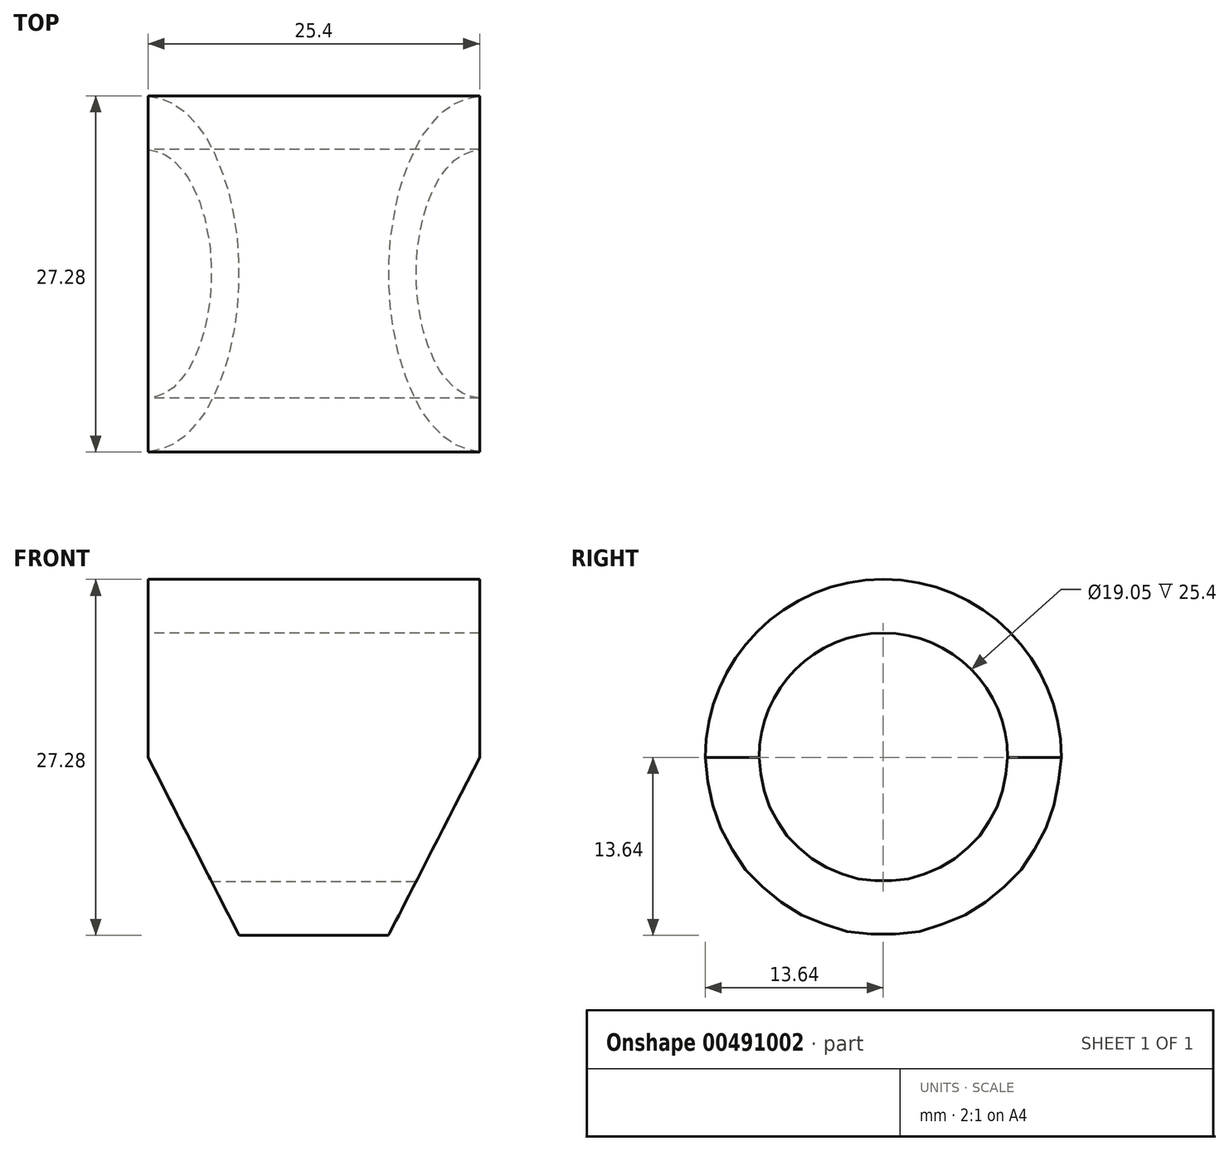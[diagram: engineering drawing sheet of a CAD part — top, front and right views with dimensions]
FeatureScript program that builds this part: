
annotation { "Feature Type Name" : "Feature", "Feature Type Description" : "" }
export const myFeature = defineFeature(function(context is Context, id is Id, definition is map)
    precondition{}
    {
        {
            var Q0;
            Q0=qCreatedBy(makeId("Right.planeOp"),FACE);
            var sketch = newSketch(context, id + "F0", { "sketchPlane" : qUnion([Q0])});
            skCircle(sketch, "E0", {"center": v(0, 0) * mm, "radius": 13.64 * mm});
            skCircle(sketch, "E1", {"center": v(0, 0) * mm, "radius": 9.53 * mm});
            skSolve(sketch);
        }
        {
            var Q0;
            Q0=makeQuery(id+"F0.imprint","IMPRINT",FACE,{"disambiguationData":[TD([[makeQuery(id+"F0.imprint","IMPRINT",EDGE,{"derivedFrom":sQuery(id+"F0.wireOp",EDGE,"E0")}),1.0]])]});
            extrude(context, id + "F1", {"entities" : qUnion([Q0]), "endBound" : BoundingType.SYMMETRIC, "depth" : 25.4 * mm});
        }
        {
            var Q0;
            Q0=qCreatedBy(makeId("Front.planeOp"),FACE);
            var sketch = newSketch(context, id + "F2", { "sketchPlane" : qUnion([Q0])});
            skLineSegment(sketch, "E2", {"start": v(-12.7, 0) * mm, "end": v(0, -24.8) * mm});
            skLineSegment(sketch, "E3", {"start": v(0, -24.8) * mm, "end": v(12.7, 0) * mm});
            skLineSegment(sketch, "E4", {"start": v(12.7, 0) * mm, "end": v(38.1, -37.9) * mm});
            skLineSegment(sketch, "E5", {"start": v(38.23, -37.66) * mm, "end": v(-20.1, -37.9) * mm});
            skLineSegment(sketch, "E6", {"start": v(-20.1, -37.9) * mm, "end": v(-12.7, 0) * mm});
            skLineSegment(sketch, "E7", {"start": v(-12.7, 0) * mm, "end": v(12.7, 0) * mm, "construction": true});
            skLineSegment(sketch, "E8", {"start": v(-5.71, -13.64) * mm, "end": v(5.72, -13.64) * mm, "construction": true});
            skLineSegment(sketch, "E9", {"start": v(0, -13.64) * mm, "end": v(0, 0) * mm, "construction": true});
            skSolve(sketch);
        }
        {
            var Q0;
            Q0 = qSketchRegion(id + "F2", true);
            extrude(context, id + "F3", {"entities" : qUnion([Q0]), "operationType" : NewBodyOperationType.REMOVE, "endBound" : BoundingType.SYMMETRIC, "oppositeDirection" : true, "depth" : 31.5 * mm});
        }
    });
